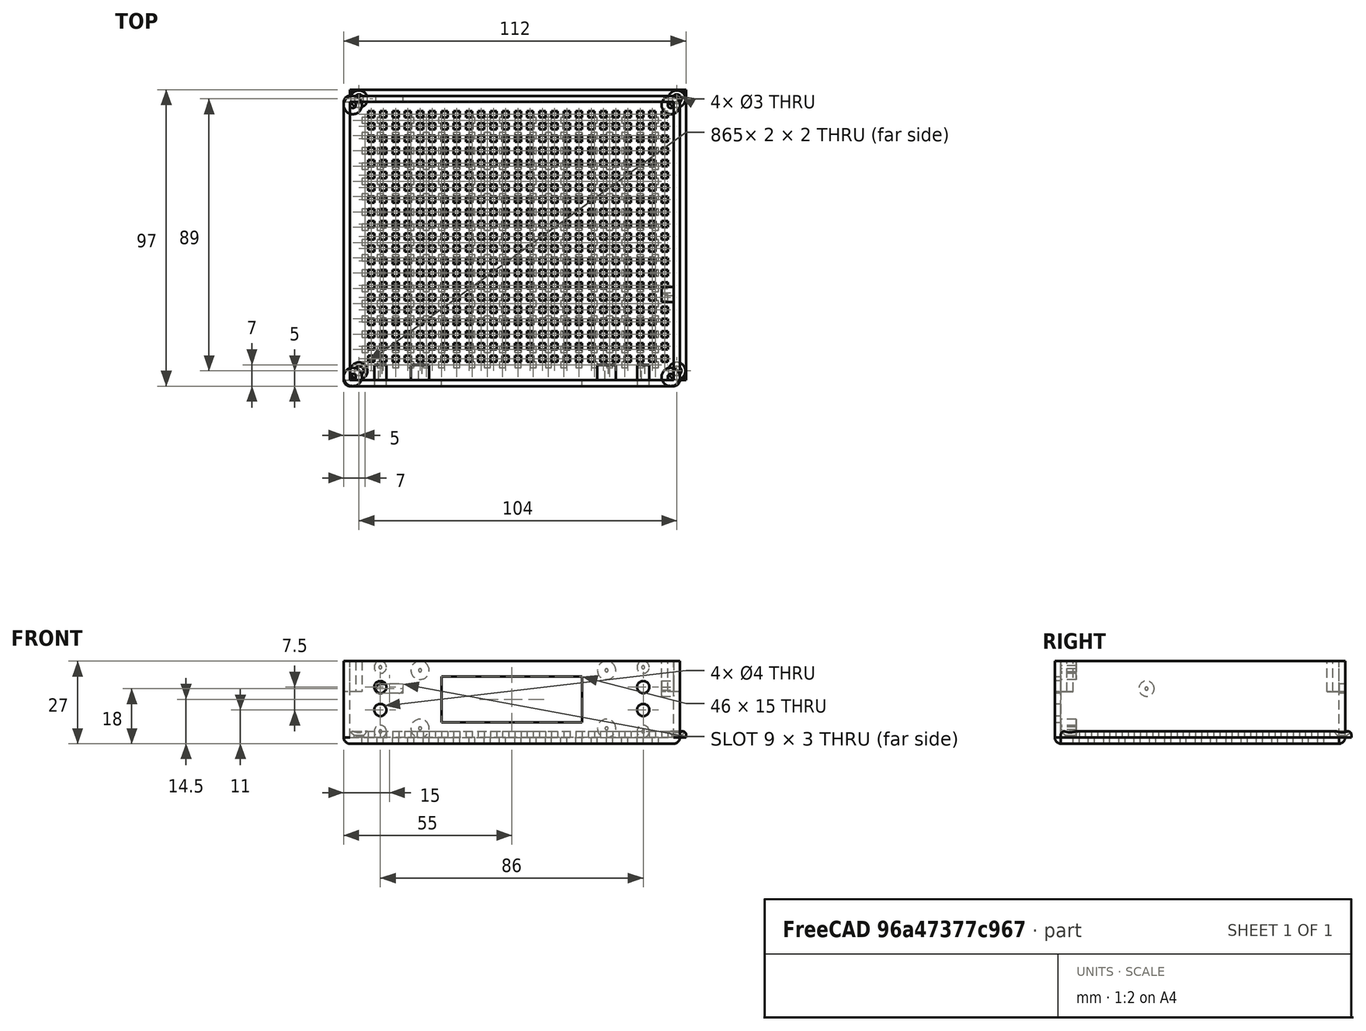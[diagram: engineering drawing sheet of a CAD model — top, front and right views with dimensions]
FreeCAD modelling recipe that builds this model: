
FCSTD DOCUMENT  (FreeCAD 1.0R39285 (Git))
Label: Clock7
License: All rights reserved
LicenseURL: https://en.wikipedia.org/wiki/All_rights_reserved
objects: Sketcher::SketchObject×9, PartDesign::Pocket×5, PartDesign::LinearPattern×4, Part::Extrusion×3, PartDesign::MultiTransform×2, Part::Compound×2, PartDesign::Body×2, Mesh::Feature×2, Part::Box×1, Part::Thickness×1, PartDesign::FeatureBase×1, PartDesign::Pad×1, PartDesign::Fillet×1, PartDesign::Chamfer×1
note: 65 computed .brp shape members not serialized (recipe doc carries the construction recipe); baked Part::Feature solids carry a one-line shape summary decoded from their .brp

FEATURE [Part::Box] Box  label="Куб"
  AttacherType = Attacher::AttachEngine3D
  Height = 25
  Length = 106
  Width = 91
FEATURE [Part::Thickness] Thickness
  Faces = -> Box [Face6]
  Intersection = false
  Join = 0
  Mode = 0
  SelfIntersection = false
  Value = 2
FEATURE [PartDesign::FeatureBase] BaseFeature
  BaseFeature = -> Thickness
  Suppressed = false
FEATURE [Sketcher::SketchObject] Sketch
  ArcFitTolerance = 1e-06
  AttachmentSupport = -> [BaseFeature]
  FullyConstrained = true
  MakeInternals = false
  MapMode = 5
  Placement = pos=(0,0,-2) rot=(1,0,0;3.14159rad)
  sketch-geometry (4):
    g0: LineSegment StartX=4 StartY=-4 StartZ=0 EndX=4 EndY=-6 EndZ=0
    g1: LineSegment StartX=4 StartY=-6 StartZ=0 EndX=6 EndY=-6 EndZ=0
    g2: LineSegment StartX=6 StartY=-6 StartZ=0 EndX=6 EndY=-4 EndZ=0
    g3: LineSegment StartX=6 StartY=-4 StartZ=0 EndX=4 EndY=-4 EndZ=0
  constraints (12):
    c: Coincident(g0,g1)
    c: Coincident(g1,g2)
    c: Coincident(g2,g3)
    c: Coincident(g3,g0)
    c: Vertical(g0)
    c: Vertical(g2)
    c: Horizontal(g1)
    c: Horizontal(g3)
    c: Distance(g0,g2) = 2
    c: Distance(g1,g3) = 2
    c: Distance(g0,g-2) = 4
    c: DistanceY(g0,g-1) = 4
FEATURE [PartDesign::Pocket] Pocket
  BaseFeature = -> BaseFeature
  Direction = (0,0,1)
  Length = 5
  Length2 = 5
  Profile = -> Sketch
  ReferenceAxis = -> Sketch [N_Axis]
  Refine = true
  Suppressed = false
  Type = 1
FEATURE [PartDesign::LinearPattern] LinearPattern
  Direction = -> X_Axis001
  Length = 95
  Mode = 1
  Occurrences = 20
  Offset = 5
  Refine = true
  Suppressed = false
  TransformMode = 0
FEATURE [PartDesign::LinearPattern] LinearPattern001
  Direction = -> Y_Axis001
  Length = 80
  Mode = 1
  Occurrences = 17
  Offset = 5
  Refine = true
  Suppressed = false
  TransformMode = 0
FEATURE [PartDesign::MultiTransform] MultiTransform
  BaseFeature = -> Pocket
  Originals = -> [Pocket]
  Refine = true
  Suppressed = false
  TransformMode = 0
  Transformations = -> [LinearPattern,LinearPattern001]
FEATURE [Sketcher::SketchObject] Sketch001
  ArcFitTolerance = 1e-06
  AttachmentSupport = -> [MultiTransform]
  FullyConstrained = true
  MakeInternals = false
  MapMode = 5
  Placement = pos=(0,-2,0) rot=(1,0,0;1.5708rad)
  sketch-geometry (8):
    g0: LineSegment StartX=30 StartY=20 StartZ=0 EndX=30 EndY=5 EndZ=0
    g1: LineSegment StartX=30 StartY=5 StartZ=0 EndX=76 EndY=5 EndZ=0
    g2: LineSegment StartX=76 StartY=5 StartZ=0 EndX=76 EndY=20 EndZ=0
    g3: LineSegment StartX=76 StartY=20 StartZ=0 EndX=30 EndY=20 EndZ=0
    g4: Circle CenterX=10 CenterY=9 CenterZ=0 NormalX=0 NormalY=0 NormalZ=1 AngleXU=0 Radius=2
    g5: Circle CenterX=10 CenterY=16.5 CenterZ=0 NormalX=0 NormalY=0 NormalZ=1 AngleXU=0 Radius=2
    g6: Circle CenterX=96 CenterY=16.5 CenterZ=0 NormalX=0 NormalY=0 NormalZ=1 AngleXU=0 Radius=2
    g7: Circle CenterX=96 CenterY=9 CenterZ=0 NormalX=0 NormalY=0 NormalZ=1 AngleXU=0 Radius=2
  constraints (24):
    c: Coincident(g0,g1)
    c: Coincident(g1,g2)
    c: Coincident(g2,g3)
    c: Coincident(g3,g0)
    c: Vertical(g0)
    c: Vertical(g2)
    c: Horizontal(g1)
    c: Horizontal(g3)
    c: DistanceX(g-1,g0) = 30
    c: Distance(g0,g-1) = 5
    c: DistanceY(g0,g0) = 15
    c: DistanceX(g0,g2) = 46
    c: Diameter(g4) = 4
    c: Diameter(g5) = 4
    c: Diameter(g6) = 4
    c: Diameter(g7) = 4
    c: DistanceX(g-1,g4) = 10
    c: Vertical(g5,g4)
    c: Horizontal(g7,g4)
    c: Vertical(g6,g7)
    c: Horizontal(g6,g5)
    c: DistanceY(g-1,g4) = 9
    c: DistanceY(g4,g5) = 7.5
    c: DistanceX(g-1,g7) = 96
FEATURE [PartDesign::Pocket] Pocket001
  BaseFeature = -> MultiTransform
  Direction = (0,1,-2e-16)
  Length = 2
  Length2 = 5
  Profile = -> Sketch001
  ReferenceAxis = -> Sketch001 [N_Axis]
  Refine = true
  Suppressed = false
  Type = 0
FEATURE [Sketcher::SketchObject] Sketch002
  ArcFitTolerance = 1e-06
  AttachmentSupport = -> [Pocket001]
  FullyConstrained = true
  MakeInternals = false
  MapMode = 5
  Placement = pos=(0,0,0) rot=(0,0.707107,0.707107;3.14159rad)
  sketch-geometry (16):
    g0: Circle CenterX=-10 CenterY=2 CenterZ=0 NormalX=0 NormalY=0 NormalZ=1 AngleXU=0 Radius=0.5
    g1: Circle CenterX=-10 CenterY=2 CenterZ=0 NormalX=0 NormalY=0 NormalZ=1 AngleXU=0 Radius=2
    g2: Circle CenterX=-23 CenterY=3 CenterZ=0 NormalX=0 NormalY=0 NormalZ=1 AngleXU=0 Radius=0.5
    g3: Circle CenterX=-23 CenterY=22 CenterZ=0 NormalX=0 NormalY=0 NormalZ=1 AngleXU=0 Radius=0.5
    g4: Circle CenterX=-23 CenterY=3 CenterZ=0 NormalX=0 NormalY=0 NormalZ=1 AngleXU=0 Radius=3
    g5: Circle CenterX=-84 CenterY=3 CenterZ=0 NormalX=0 NormalY=0 NormalZ=1 AngleXU=0 Radius=0.5
    g6: Circle CenterX=-84 CenterY=22 CenterZ=0 NormalX=0 NormalY=0 NormalZ=1 AngleXU=0 Radius=0.5
    g7: Circle CenterX=-23 CenterY=22 CenterZ=0 NormalX=0 NormalY=0 NormalZ=1 AngleXU=0 Radius=3
    g8: Circle CenterX=-84 CenterY=22 CenterZ=0 NormalX=0 NormalY=0 NormalZ=1 AngleXU=0 Radius=3
    g9: Circle CenterX=-84 CenterY=3 CenterZ=0 NormalX=0 NormalY=0 NormalZ=1 AngleXU=0 Radius=3
    g10: Circle CenterX=-10 CenterY=23 CenterZ=0 NormalX=0 NormalY=0 NormalZ=1 AngleXU=0 Radius=0.5
    g11: Circle CenterX=-10 CenterY=23 CenterZ=0 NormalX=0 NormalY=0 NormalZ=1 AngleXU=0 Radius=2
    g12: Circle CenterX=-95.9792 CenterY=2 CenterZ=0 NormalX=0 NormalY=0 NormalZ=1 AngleXU=0 Radius=0.5
    g13: Circle CenterX=-95.9792 CenterY=23 CenterZ=0 NormalX=0 NormalY=0 NormalZ=1 AngleXU=0 Radius=0.5
    g14: Circle CenterX=-95.9792 CenterY=2 CenterZ=0 NormalX=0 NormalY=0 NormalZ=1 AngleXU=0 Radius=2
    g15: Circle CenterX=-95.9792 CenterY=23 CenterZ=0 NormalX=0 NormalY=0 NormalZ=1 AngleXU=0 Radius=2
  constraints (40):
    c: Diameter(g0) = 1
    c: Diameter(g1) = 4
    c: Coincident(g1,g0)
    c: DistanceX(g0,g-1) = 10
    c: DistanceY(g-1,g0) = 2
    c: Diameter(g2) = 1
    c: Diameter(g3) = 1
    c: Diameter(g4) = 6
    c: Coincident(g4,g2)
    c: DistanceX(g2,g-1) = 23
    c: DistanceY(g-1,g2) = 3
    c: Diameter(g5) = 1
    c: Diameter(g6) = 1
    c: DistanceX(g5,g-1) = 84
    c: Vertical(g6,g5)
    c: Vertical(g2,g3)
    c: Horizontal(g3,g6)
    c: Horizontal(g5,g2)
    c: Diameter(g7) = 6
    c: Coincident(g7,g3)
    c: Diameter(g8) = 6
    c: Coincident(g8,g6)
    c: Diameter(g9) = 6
    c: Coincident(g9,g5)
    c: DistanceY(g-1,g3) = 22
    c: Diameter(g10) = 1
    c: Diameter(g11) = 4
    c: Coincident(g11,g10)
    c: DistanceY(g-1,g10) = 23
    c: Vertical(g10,g0)
    c: Diameter(g12) = 1
    c: Diameter(g13) = 1
    c: Vertical(g13,g12)
    c: Horizontal(g13,g10)
    c: Horizontal(g0,g12)
    c: Distance(g12,g-1) = 96
    c: Diameter(g14) = 4
    c: Coincident(g14,g12)
    c: Diameter(g15) = 4
    c: Coincident(g15,g13)
FEATURE [Part::Extrusion] Extrude
  Base = -> Sketch002
  Dir = (0,1,-2e-16)
  DirMode = 2
  FaceMakerClass = Part::FaceMakerBullseye
  FaceMakerMode = 3
  LengthFwd = 5
  LengthRev = 0
  Solid = true
  Symmetric = false
FEATURE [Sketcher::SketchObject] Sketch003
  ArcFitTolerance = 1e-06
  AttachmentSupport = -> [Pocket001]
  FullyConstrained = true
  MakeInternals = false
  MapMode = 5
  Placement = pos=(0,93,0) rot=(0,0.707107,0.707107;3.14159rad)
  sketch-geometry (4):
    g0: ArcOfCircle CenterX=-16 CenterY=16 CenterZ=0 NormalX=0 NormalY=0 NormalZ=1 AngleXU=0 Radius=1.5 StartAngle=1.5708 EndAngle=4.71239
    g1: ArcOfCircle CenterX=-10 CenterY=16 CenterZ=0 NormalX=0 NormalY=0 NormalZ=1 AngleXU=0 Radius=1.5 StartAngle=4.71239 EndAngle=7.85398
    g2: LineSegment StartX=-16 StartY=17.5 StartZ=0 EndX=-10 EndY=17.5 EndZ=0
    g3: LineSegment StartX=-16 StartY=14.5 StartZ=0 EndX=-10 EndY=14.5 EndZ=0
  constraints (10):
    c: Tangent(g0,g2) = 1.5708
    c: Tangent(g0,g3) = -1.5708
    c: Tangent(g1,g2) = 1.5708
    c: Tangent(g1,g3) = -1.5708
    c: Equal(g0,g1)
    c: Horizontal(g3)
    c: Distance(g0,g1) = 6
    c: Radius(g0) = 1.5
    c: DistanceX(g1,g-1) = 10
    c: DistanceY(g-1,g1) = 16
FEATURE [Sketcher::SketchObject] Sketch005
  ArcFitTolerance = 1e-06
  FullyConstrained = true
  MakeInternals = false
  MapMode = 5
  Placement = pos=(106,0,0) rot=(0.57735,-0.57735,-0.57735;2.0944rad)
  sketch-geometry (2):
    g0: Circle CenterX=-28 CenterY=16 CenterZ=0 NormalX=0 NormalY=0 NormalZ=1 AngleXU=0 Radius=0.5
    g1: Circle CenterX=-28 CenterY=16 CenterZ=0 NormalX=0 NormalY=0 NormalZ=1 AngleXU=0 Radius=2.5
  constraints (5):
    c: Diameter(g0) = 1
    c: DistanceY(g-1,g0) = 16
    c: DistanceX(g0,g-1) = 28
    c: Diameter(g1) = 5
    c: Coincident(g1,g0)
FEATURE [Part::Extrusion] Extrude002
  Base = -> Sketch005
  Dir = (-1,0,0)
  DirMode = 2
  FaceMakerClass = Part::FaceMakerBullseye
  FaceMakerMode = 3
  LengthFwd = 4
  LengthRev = 0
  Solid = true
  Symmetric = false
FEATURE [Sketcher::SketchObject] Sketch006
  ArcFitTolerance = 1e-06
  FullyConstrained = true
  MakeInternals = false
  MapMode = 5
  Placement = pos=(0,0,25) rot=(0,0,1;0rad)
  sketch-geometry (8):
    g0: Circle CenterX=1 CenterY=1 CenterZ=0 NormalX=0 NormalY=0 NormalZ=1 AngleXU=0 Radius=1
    g1: Circle CenterX=1 CenterY=1 CenterZ=0 NormalX=0 NormalY=0 NormalZ=1 AngleXU=0 Radius=3
    g2: Circle CenterX=1 CenterY=90 CenterZ=0 NormalX=0 NormalY=0 NormalZ=1 AngleXU=0 Radius=1
    g3: Circle CenterX=1 CenterY=90 CenterZ=0 NormalX=0 NormalY=0 NormalZ=1 AngleXU=0 Radius=3
    g4: Circle CenterX=104.995 CenterY=90 CenterZ=0 NormalX=0 NormalY=0 NormalZ=1 AngleXU=0 Radius=1
    g5: Circle CenterX=104.995 CenterY=90 CenterZ=0 NormalX=0 NormalY=0 NormalZ=1 AngleXU=0 Radius=3
    g6: Circle CenterX=104.995 CenterY=1 CenterZ=0 NormalX=0 NormalY=0 NormalZ=1 AngleXU=0 Radius=1
    g7: Circle CenterX=104.995 CenterY=1 CenterZ=0 NormalX=0 NormalY=0 NormalZ=1 AngleXU=0 Radius=3
  constraints (20):
    c: Diameter(g0) = 2
    c: Diameter(g1) = 6
    c: Coincident(g1,g0)
    c: DistanceY(g-1,g0) = 1
    c: DistanceX(g-1,g0) = 1
    c: Diameter(g2) = 2
    c: DistanceY(g-1,g2) = 90
    c: Diameter(g3) = 6
    c: Coincident(g3,g2)
    c: Vertical(g2,g0)
    c: Diameter(g4) = 2
    c: Diameter(g5) = 6
    c: Coincident(g5,g4)
    c: Diameter(g6) = 2
    c: Diameter(g7) = 6
    c: Coincident(g7,g6)
    c: Vertical(g6,g4)
    c: Horizontal(g4,g2)
    c: Horizontal(g6,g0)
    c: Distance(g6,g-1) = 105
FEATURE [Part::Extrusion] Extrude003
  Base = -> Sketch006
  Dir = (0,0,1)
  DirMode = 2
  FaceMakerClass = Part::FaceMakerBullseye
  FaceMakerMode = 3
  LengthFwd = 10
  LengthRev = 0
  Reversed = true
  Solid = true
  Symmetric = false
FEATURE [Part::Compound] Compound
  Links = -> [Extrude,Extrude002,Extrude003]
FEATURE [PartDesign::Pocket] Pocket002
  BaseFeature = -> Pocket001
  Direction = (0,-1,2e-16)
  Length = 2
  Length2 = 5
  Profile = -> Sketch003
  ReferenceAxis = -> Sketch003 [N_Axis]
  Refine = true
  Suppressed = false
  Type = 0
FEATURE [PartDesign::Body] Body001  label="Тело001"
  AllowCompound = false
  BaseFeature = -> Thickness
  Group = -> [BaseFeature,Sketch,Pocket,MultiTransform,LinearPattern,LinearPattern001,Sketch001,Pocket001,Sketch002,Sketch003,Sketch005,Sketch006,Pocket002]
  Origin = -> Origin001
  Tip = -> Pocket002
FEATURE [Part::Compound] Compound001  label="box"
  Links = -> [Body001,Compound]
FEATURE [Sketcher::SketchObject] Sketch007
  ArcFitTolerance = 1e-06
  AttachmentSupport = -> [XY_Plane]
  FullyConstrained = true
  MakeInternals = false
  MapMode = 5
  sketch-geometry (4):
    g0: LineSegment StartX=0 StartY=0 StartZ=0 EndX=110 EndY=0 EndZ=0
    g1: LineSegment StartX=110 StartY=0 StartZ=0 EndX=110 EndY=95 EndZ=0
    g2: LineSegment StartX=110 StartY=95 StartZ=0 EndX=0 EndY=95 EndZ=0
    g3: LineSegment StartX=0 StartY=95 StartZ=0 EndX=0 EndY=0 EndZ=0
  constraints (11):
    c: Coincident(g0,g1)
    c: Coincident(g1,g2)
    c: Coincident(g2,g3)
    c: Coincident(g3,g0)
    c: Horizontal(g0)
    c: Horizontal(g2)
    c: Vertical(g1)
    c: Vertical(g3)
    c: Coincident(g0,g-1)
    c: DistanceX(g0,g0) = 110
    c: Distance(g2,g-1) = 95
FEATURE [PartDesign::Pad] Pad
  Direction = (0,0,1)
  Length = 2
  Length2 = 10
  Profile = -> Sketch007
  ReferenceAxis = -> Sketch007 [N_Axis]
  Refine = true
  Suppressed = false
  Type = 0
FEATURE [PartDesign::Fillet] Fillet
  Base = -> Pad [Face6]
  BaseFeature = -> Pad
  Radius = 1
  Refine = true
  SupportTransform = false
  Suppressed = false
  UseAllEdges = false
FEATURE [Sketcher::SketchObject] Sketch008
  ArcFitTolerance = 1e-06
  AttachmentSupport = -> [Fillet]
  FullyConstrained = true
  MakeInternals = false
  MapMode = 5
  Placement = pos=(0,0,2) rot=(0,0,1;0rad)
  sketch-geometry (4):
    g0: Circle CenterX=3 CenterY=3 CenterZ=0 NormalX=0 NormalY=0 NormalZ=1 AngleXU=0 Radius=1.5
    g1: Circle CenterX=107 CenterY=3 CenterZ=0 NormalX=0 NormalY=0 NormalZ=1 AngleXU=0 Radius=1.5
    g2: Circle CenterX=107 CenterY=92 CenterZ=0 NormalX=0 NormalY=0 NormalZ=1 AngleXU=0 Radius=1.5
    g3: Circle CenterX=3 CenterY=92 CenterZ=0 NormalX=0 NormalY=0 NormalZ=1 AngleXU=0 Radius=1.5
  constraints (12):
    c: Diameter(g0) = 3
    c: Diameter(g1) = 3
    c: Diameter(g2) = 3
    c: Diameter(g3) = 3
    c: DistanceY(g-1,g3) = 92
    c: Horizontal(g3,g2)
    c: Vertical(g2,g1)
    c: DistanceX(g-1,g0) = 3
    c: DistanceX(g-1,g1) = 107
    c: Vertical(g3,g0)
    c: Horizontal(g0,g1)
    c: DistanceY(g-1,g0) = 3
FEATURE [PartDesign::Pocket] Pocket003
  BaseFeature = -> Fillet
  Direction = (0,0,-1)
  Length = 2
  Length2 = 5
  Profile = -> Sketch008
  ReferenceAxis = -> Sketch008 [N_Axis]
  Refine = true
  Suppressed = false
  Type = 0
FEATURE [PartDesign::Chamfer] Chamfer
  Angle = 45
  Base = -> Pocket003 [Edge26,Edge27,Edge25,Edge24]
  BaseFeature = -> Pocket003
  ChamferType = 0
  FlipDirection = false
  Refine = true
  Size = 1.3
  Size2 = 1
  SupportTransform = false
  Suppressed = false
  UseAllEdges = false
FEATURE [Sketcher::SketchObject] Sketch009
  ArcFitTolerance = 1e-06
  AttachmentSupport = -> [Chamfer]
  FullyConstrained = true
  MakeInternals = false
  MapMode = 5
  Placement = pos=(0,0,2) rot=(0,0,1;0rad)
  sketch-geometry (4):
    g0: LineSegment StartX=6 StartY=6 StartZ=0 EndX=8 EndY=6 EndZ=0
    g1: LineSegment StartX=8 StartY=6 StartZ=0 EndX=8 EndY=8 EndZ=0
    g2: LineSegment StartX=8 StartY=8 StartZ=0 EndX=6 EndY=8 EndZ=0
    g3: LineSegment StartX=6 StartY=8 StartZ=0 EndX=6 EndY=6 EndZ=0
  constraints (12):
    c: Coincident(g0,g1)
    c: Coincident(g1,g2)
    c: Coincident(g2,g3)
    c: Coincident(g3,g0)
    c: Horizontal(g0)
    c: Horizontal(g2)
    c: Vertical(g1)
    c: Vertical(g3)
    c: Distance(g1,g3) = 2
    c: Distance(g0,g2) = 2
    c: DistanceX(g-1,g0) = 6
    c: DistanceY(g-1,g0) = 6
FEATURE [PartDesign::Pocket] Pocket004
  BaseFeature = -> Chamfer
  Direction = (0,0,-1)
  Length = 2
  Length2 = 5
  Profile = -> Sketch009
  ReferenceAxis = -> Sketch009 [N_Axis]
  Refine = true
  Suppressed = false
  Type = 0
FEATURE [PartDesign::LinearPattern] LinearPattern002
  Direction = -> Sketch009 [H_Axis]
  Length = 96
  Mode = 1
  Occurrences = 25
  Offset = 4
  Refine = true
  Suppressed = false
  TransformMode = 0
FEATURE [PartDesign::LinearPattern] LinearPattern003
  Direction = -> Sketch009 [V_Axis]
  Length = 80
  Mode = 1
  Occurrences = 21
  Offset = 4
  Refine = true
  Suppressed = false
  TransformMode = 0
FEATURE [PartDesign::MultiTransform] MultiTransform001
  BaseFeature = -> Pocket004
  Originals = -> [Pocket004]
  Refine = true
  Suppressed = false
  TransformMode = 0
  Transformations = -> [LinearPattern002,LinearPattern003]
FEATURE [PartDesign::Body] Body  label="cap"
  AllowCompound = false
  Group = -> [Sketch007,Pad,Fillet,Sketch008,Pocket003,Chamfer,Sketch009,Pocket004,MultiTransform001,LinearPattern002,LinearPattern003]
  Origin = -> Origin
  Tip = -> MultiTransform001
FEATURE [Mesh::Feature] Mesh  label="box (Meshed)"
FEATURE [Mesh::Feature] Mesh001  label="cap (Meshed)"
